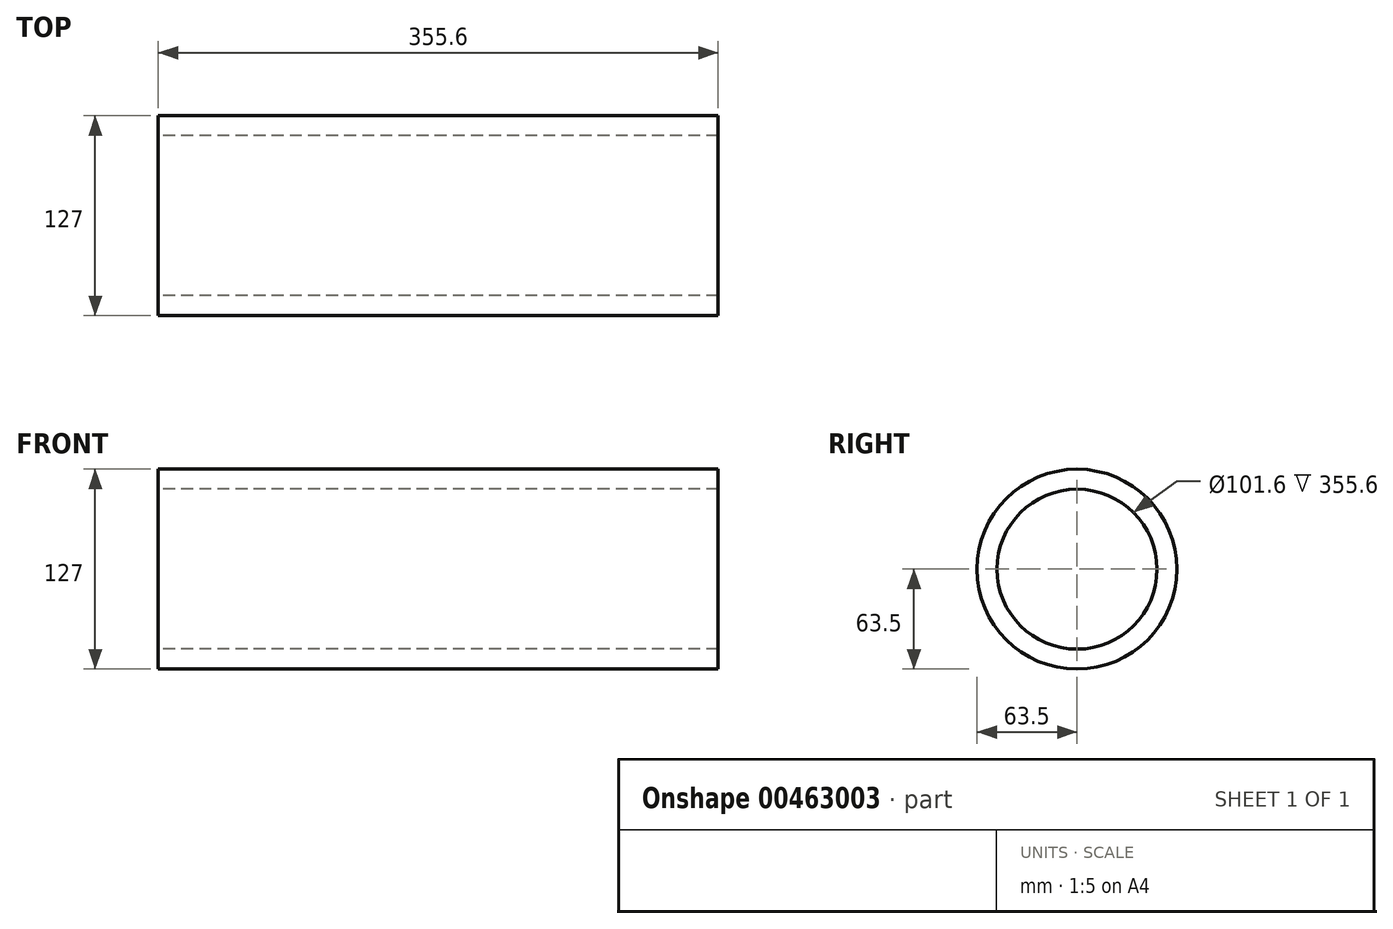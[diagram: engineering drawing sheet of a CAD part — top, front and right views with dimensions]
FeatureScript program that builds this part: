
annotation { "Feature Type Name" : "Feature", "Feature Type Description" : "" }
export const myFeature = defineFeature(function(context is Context, id is Id, definition is map)
    precondition{}
    {
        {
            var Q0;
            Q0=qCreatedBy(makeId("Right.planeOp"),FACE);
            var sketch = newSketch(context, id + "F0", { "sketchPlane" : qUnion([Q0])});
            skCircle(sketch, "E0", {"center": v(0, 0) * mm, "radius": 63.5 * mm});
            skCircle(sketch, "E1", {"center": v(0, 0) * mm, "radius": 50.8 * mm});
            skSolve(sketch);
        }
        {
            var Q0;
            Q0=makeQuery(id+"F0.imprint","IMPRINT",FACE,{"disambiguationData":[TD([[makeQuery(id+"F0.imprint","IMPRINT",EDGE,{"derivedFrom":sQuery(id+"F0.wireOp",EDGE,"E0")}),1.0]])]});
            extrude(context, id + "F1", {"entities" : qUnion([Q0]), "depth" : 355.6 * mm});
        }
    });
